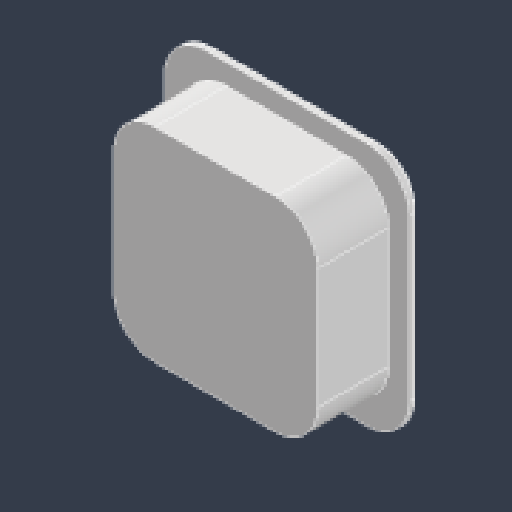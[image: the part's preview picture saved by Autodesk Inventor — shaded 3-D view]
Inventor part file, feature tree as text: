
AUTODESK INVENTOR PART (.ipt)
format: ipt  version: 2023.4 (Build 274418000, 418)  size: 123,392 bytes
history: native  units: mm
features: extrude x2, sketch x2, fillet x1, chamfer x1
ambient origin geometry x8: Origin, YZ Plane, XZ Plane, XY Plane, X Axis, Y Axis, Z Axis, Center Point
bodies: Solid1 (feature_tree)
feature tree (6):
  extrude  "Extrusion1"  Depth=24.0mm
  extrude  "Extrusion2"  Depth=20.0mm
  fillet  "Fillet1"  Radius=20.0mm
  chamfer  "Chamfer1"  Distance=7.0mm
  sketch  "Sketch1"  dims[d0=24.0mm d1=24.0mm]
  sketch  "Sketch2"  dims[d2=1.0mm d3=0.0mm d4=20.0mm d5=20.0mm d6=7.0mm d7=0.0mm d8=4.1mm d9=0.4mm d10=2.0mm d11=45.0deg]
